# Revit family: IS_Solea_R0133_BIM_DE
name_source: partatom
category: Plumbing Fixtures
revit_build: Autodesk Revit 2017 (Build: 20171027_0315(x64)
units: mm (PartAtom-declared; Revit-internal decimal feet)

## family parameters
Cut with Voids When Loaded = No
Host = Face
OmniClass Number = 23.45.05.21.11.11
OmniClass Title = Water Operated Water Closets
Part Type = Normal
Room Calculation Point = No
Round Connector Dimension = Use Diameter
Shared = Yes

## types (3) — shared parameters
Afmetingen = 215 x 145 x 16 mm
AfstandsEenheid = millimeters
Artikelreferentie = 1
Assembly Code = C1030200
Auteur = Ideal Standrad
BREEAMApproved = No
Beschrijvinggarantie = Manufacturers Warranty
Default Elevation = 900 mm
Douchebak = No
DuurEenheid = year
ECA = No
Garantieunits = Year
Heefthandvaten = No
Hulp = https://www.idealstandard.de
Installatieinstructies = https://www.idealstandard.de
Materiaal = Metal
Merk = Ideal Standard
Montageinstuctie = https://www.idealstandard.de
NBSDescription = WC cistern fittings
NBSReference = 45-30-70/387
Nettogewicht = 0.3769
Productinformatie = https://www.idealstandard.de
Telefoonnummer = +49 (0) 6571 16 0
URL = https://www.idealstandard.de
Uniclass2 = Pr_40_20_93_89
Uniclass2015Description = Urinal and WC fittings
Uniclass2015Referentie = Pr_40_20_93
Urlproducent = https://www.idealstandard.de
Versie = 1
Verwachtelevensduur = 5
Volumeunits = Litres
WRAS = No
WaterEfficientProduct = No
zero-valued in all types: Breedte, BrutoGewicht, CWFU, Cost, Diepte, GrootteAfvoergat, HWFU, Lengte, Overloop, Vervangingskosten, WFU

## per-type parameters (varying)
| type | Afwerking | Artikelnummer | Artikelomschrijving | Barcode | BimObjectNaam | Kleur | Model |
| R0133AC - SALINA P1 WHITE - IS | White | R0133AC | Betätigungsplatte P1 SOLEA, mechanischen Auslösung, Chrom | 3391500580602 | IS_Ideal Standard_WC cistern fittings_Salina_R0133AC | White | R0133AC |
| R0133AA - SALINA P1 CHROME - IS | Chrome | R0133AA | Betätigungsplatte P1 SOLEA, pneumatischen Auslösung, Chrom matt | 3391500580596 | IS_Ideal Standard_WC cistern fittings_Solea_R0133AA | Chrome | R0133AA |
| R0133JG - SALINA P1 MATT CHROME- IS | White | R0133JG | Betätigungsplatte M1 SEPTA PRO, mechanischen Auslösung, Stahl gebürstet | 3391500580619 | IS_Ideal Standard_WC cistern fittings_Salina_R0133JG | White | R0133JG |

## geometry (parser evidence)
native form markers: Sweep x4
no freeform markers — native parametric forms only
